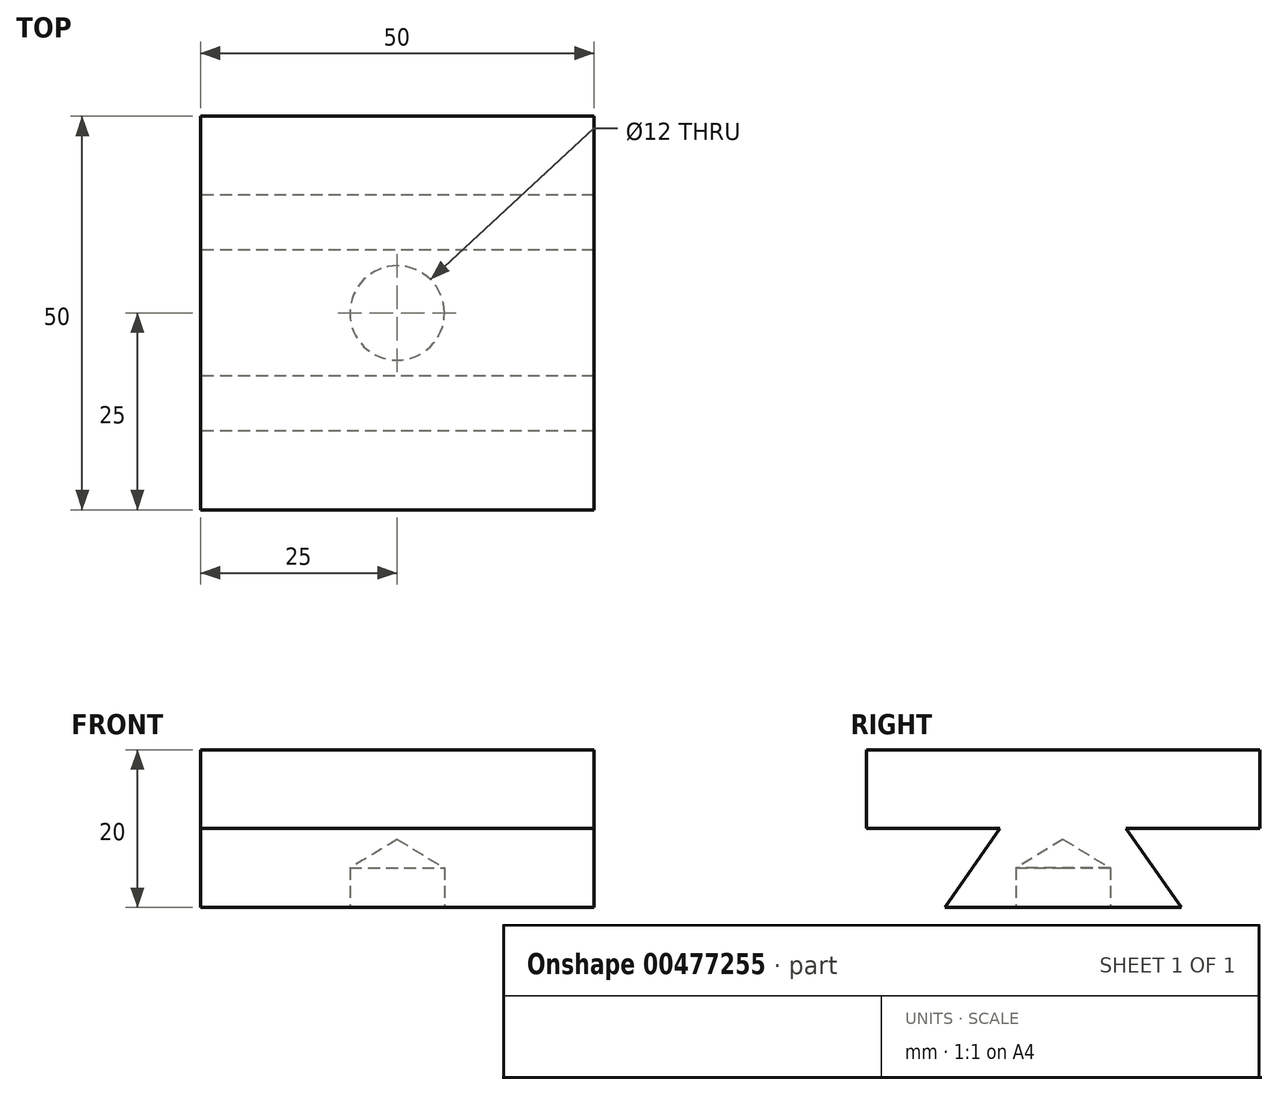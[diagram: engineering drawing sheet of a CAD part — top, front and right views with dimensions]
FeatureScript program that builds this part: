
annotation { "Feature Type Name" : "Feature", "Feature Type Description" : "" }
export const myFeature = defineFeature(function(context is Context, id is Id, definition is map)
    precondition{}
    {
        {
            var Q0;
            Q0=qCreatedBy(makeId("Top.planeOp"),FACE);
            var sketch = newSketch(context, id + "F0", { "sketchPlane" : qUnion([Q0])});
            skLineSegment(sketch, "E0.bottom", {"start": v(25, -25) * mm, "end": v(-25, -25) * mm});
            skLineSegment(sketch, "E0.top", {"start": v(25, 25) * mm, "end": v(-25, 25) * mm});
            skLineSegment(sketch, "E0.left", {"start": v(25, -25) * mm, "end": v(25, 25) * mm});
            skLineSegment(sketch, "E0.right", {"start": v(-25, -25) * mm, "end": v(-25, 25) * mm});
            skPoint(sketch, "E0.middle", {"position": v(0, 0) * mm});
            skSolve(sketch);
        }
        {
            var Q0;
            Q0=makeQuery(id+"F0.imprint","IMPRINT",FACE,{"disambiguationData":[TD([[makeQuery(id+"F0.imprint","IMPRINT",EDGE,{"derivedFrom":sQuery(id+"F0.wireOp",EDGE,"E0.bottom")}),-1.0]])]});
            extrude(context, id + "F1", {"entities" : qUnion([Q0]), "depth" : 10 * mm});
        }
        {
            var Q0;
            Q0=qCreatedBy(makeId("Right.planeOp"),FACE);
            var sketch = newSketch(context, id + "F2", { "sketchPlane" : qUnion([Q0])});
            skLineSegment(sketch, "E1", {"start": v(0, 0) * mm, "end": v(0, -10) * mm});
            skLineSegment(sketch, "E2", {"start": v(0, -10) * mm, "end": v(15, -10) * mm});
            skLineSegment(sketch, "E3", {"start": v(15, -10) * mm, "end": v(8, 0) * mm});
            skLineSegment(sketch, "E4", {"start": v(0, -10) * mm, "end": v(-15, -10) * mm});
            skLineSegment(sketch, "E5", {"start": v(-15, -10) * mm, "end": v(-8, 0) * mm});
            skLineSegment(sketch, "E6", {"start": v(8, 0) * mm, "end": v(-8, 0) * mm});
            skSolve(sketch);
        }
        {
            var Q0;
            {var subQ0=sQuery(id+"F2.wireOp",EDGE,"E1");Q0=makeQuery(id+"F2.imprint","IMPRINT",FACE,{"disambiguationData":[TD([[makeQuery(id+"F2.imprint","IMPRINT",EDGE,{"derivedFrom":subQ0}),-1.0]])]});}
            var Q1;
            {var subQ0=sQuery(id+"F2.wireOp",EDGE,"E1");Q1=makeQuery(id+"F2.imprint","IMPRINT",FACE,{"disambiguationData":[TD([[makeQuery(id+"F2.imprint","IMPRINT",EDGE,{"derivedFrom":subQ0}),1.0]])]});}
            extrude(context, id + "F3", {"entities" : qUnion([Q0, Q1]), "operationType" : NewBodyOperationType.ADD, "endBound" : BoundingType.SYMMETRIC, "depth" : 50 * mm});
        }
        {
            var Q0;
            Q0=makeQuery(id+"F3.opExtrude","SWEPT_FACE",FACE,{"disambiguationData":[OSD([sQuery(id+"F2.wireOp",EDGE,"E2"),sQuery(id+"F2.wireOp",EDGE,"E4")])]});
            var sketch = newSketch(context, id + "F4", { "sketchPlane" : qUnion([Q0])});
            skPoint(sketch, "E7", {"position": v(0, 0) * mm});
            skSolve(sketch);
        }
        {
            var Q0;
            Q0=sQuery(id+"F4.wireOp",VERTEX,"E7");
            var Q1;
            Q1=makeQuery(id+"F1.opExtrude","SWEPT_BODY",BODY,{"disambiguationData":[OSD([sQuery(id+"F0.wireOp",EDGE,"E0.bottom"),sQuery(id+"F0.wireOp",EDGE,"E0.top"),sQuery(id+"F0.wireOp",EDGE,"E0.left"),sQuery(id+"F0.wireOp",EDGE,"E0.right")])]});
            hole(context, id + "F5", {"style" : HoleStyle.SIMPLE, "endStyle" : HoleEndStyle.BLIND, "holeDiameter" : 12 * mm, "holeDepth" : 5 * mm, "isTappedThrough" : true, "tappedDepth" : 12 * mm, "tapClearance" : 3, "locations" : qUnion([Q0]), "scope" : qUnion([Q1])});
        }
    });
